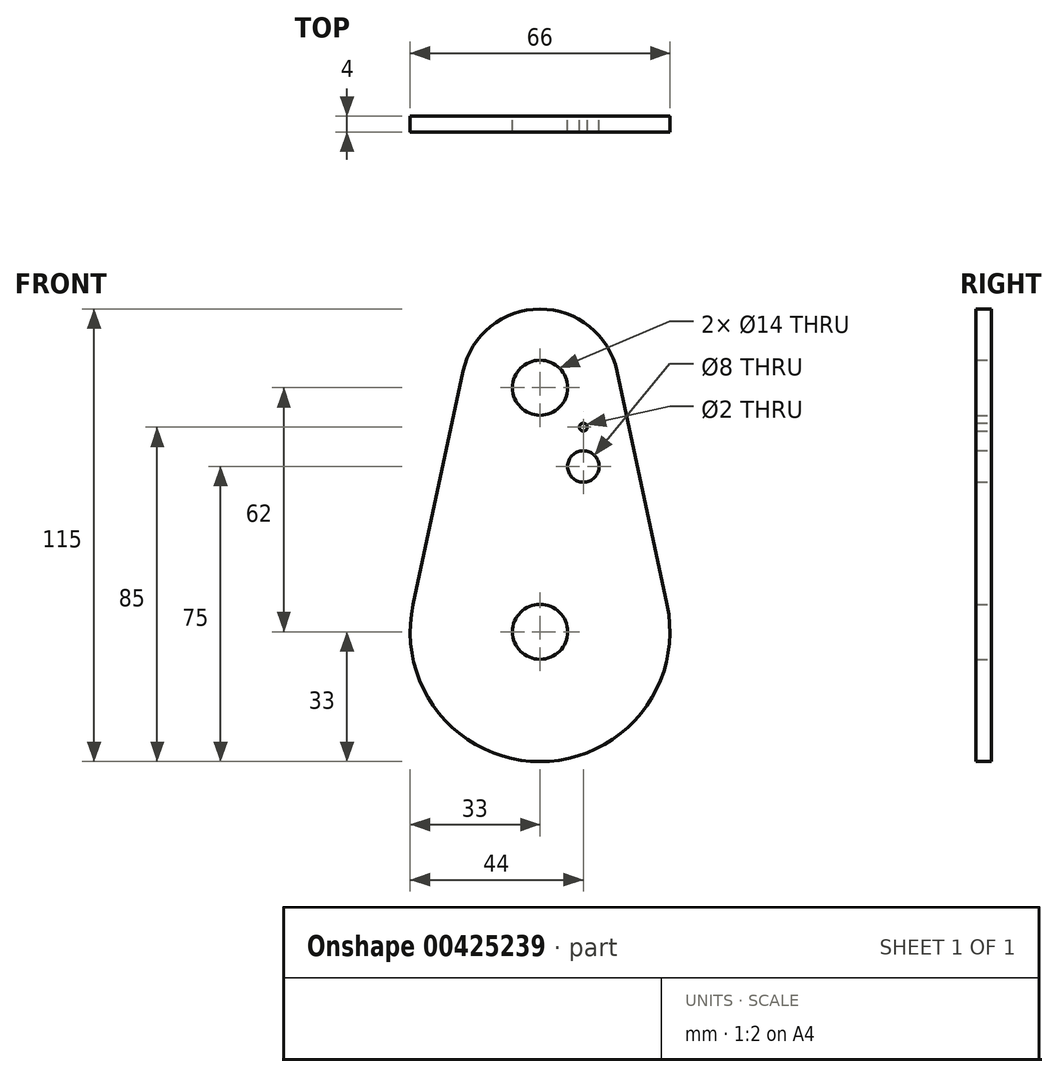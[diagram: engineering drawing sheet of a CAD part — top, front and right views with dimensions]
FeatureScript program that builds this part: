
annotation { "Feature Type Name" : "Feature", "Feature Type Description" : "" }
export const myFeature = defineFeature(function(context is Context, id is Id, definition is map)
    precondition{}
    {
        {
            var Q0;
            Q0=qCreatedBy(makeId("Front.planeOp"),FACE);
            var sketch = newSketch(context, id + "F0", { "sketchPlane" : qUnion([Q0])});
            skCircle(sketch, "E0", {"center": v(0, 0) * mm, "radius": 7 * mm});
            skCircle(sketch, "E1", {"center": v(0, 62) * mm, "radius": 7 * mm});
            skArc(sketch, "E2", {"start": v(-19.56, 66.2) * mm, "mid": v(0, 82) * mm, "end": v(19.56, 66.2) * mm});
            skArc(sketch, "E3", {"start": v(32.27, 6.92) * mm, "mid": v(0, -33) * mm, "end": v(-32.27, 6.92) * mm});
            skLineSegment(sketch, "E4", {"start": v(-19.56, 66.2) * mm, "end": v(-32.27, 6.92) * mm});
            skLineSegment(sketch, "E5", {"start": v(19.56, 66.2) * mm, "end": v(32.27, 6.92) * mm});
            skCircle(sketch, "E6", {"center": v(11, 42) * mm, "radius": 4 * mm});
            skCircle(sketch, "E7", {"center": v(11, 52) * mm, "radius": 1 * mm});
            skSolve(sketch);
        }
        {
            var Q0;
            Q0=makeQuery(id+"F0.imprint","IMPRINT",FACE,{"disambiguationData":[TD([[makeQuery(id+"F0.imprint","IMPRINT",EDGE,{"derivedFrom":sQuery(id+"F0.wireOp",EDGE,"E0")}),-1.0]])]});
            extrude(context, id + "F1", {"entities" : qUnion([Q0]), "depth" : 4 * mm});
        }
    });
